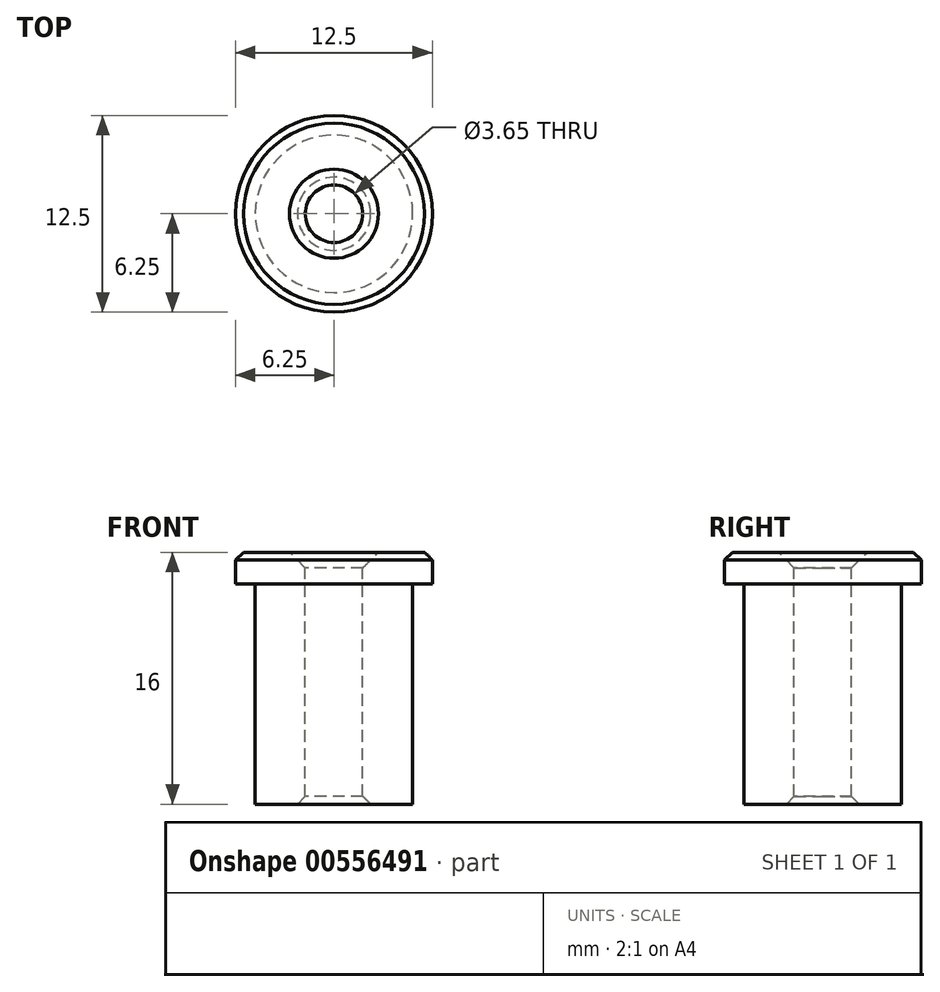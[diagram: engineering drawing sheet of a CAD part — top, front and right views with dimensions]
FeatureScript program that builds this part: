
annotation { "Feature Type Name" : "Feature", "Feature Type Description" : "" }
export const myFeature = defineFeature(function(context is Context, id is Id, definition is map)
    precondition{}
    {
        {
            var Q0;
            Q0=qCreatedBy(makeId("Top.planeOp"),FACE);
            var sketch = newSketch(context, id + "F0", { "sketchPlane" : qUnion([Q0])});
            skCircle(sketch, "E0", {"center": v(0, 0) * mm, "radius": 6.25 * mm});
            skCircle(sketch, "E1", {"center": v(0, 0) * mm, "radius": 1.82 * mm});
            skSolve(sketch);
        }
        {
            var Q0;
            Q0 = qSketchRegion(id + "F0", true);
            extrude(context, id + "F1", {"entities" : qUnion([Q0]), "oppositeDirection" : true, "depth" : 16 * mm, "offsetDistance" : 25 * mm});
        }
        {
            var Q0;
            Q0=makeQuery(id+"F1.opExtrude","CAP_EDGE",EDGE,{"disambiguationData":[OSD([sQuery(id+"F0.wireOp",EDGE,"E1")])],"isStart":true});
            chamfer(context, id + "F2", {"entities" : qUnion([Q0]), "width" : 1 * mm, "tangentPropagation" : true});
        }
        {
            var Q0;
            Q0=makeQuery(id+"F1.opExtrude","CAP_FACE",FACE,{"disambiguationData":[OSD([sQuery(id+"F0.wireOp",EDGE,"E0"),sQuery(id+"F0.wireOp",EDGE,"E1")])],"isStart":false});
            var sketch = newSketch(context, id + "F3", { "sketchPlane" : qUnion([Q0])});
            skCircle(sketch, "E2", {"center": v(0, 0) * mm, "radius": 5 * mm});
            skSolve(sketch);
        }
        {
            var Q0;
            Q0=makeQuery(id+"F3.imprint","IMPRINT",FACE,{"disambiguationData":[TD([[makeQuery(id+"F3.imprint","IMPRINT",EDGE,{"derivedFrom":sQuery(id+"F3.wireOp",EDGE,"E2")}),-1.0]])]});
            extrude(context, id + "F4", {"entities" : qUnion([Q0]), "operationType" : NewBodyOperationType.REMOVE, "oppositeDirection" : true, "depth" : 14 * mm, "offsetDistance" : 25 * mm});
        }
        {
            var Q0;
            Q0=makeQuery(id+"F4.boolean.opBoolean","COPY",EDGE,{"derivedFrom":makeQuery(id+"F4.opExtrude","CAP_EDGE",EDGE,{"disambiguationData":[OSD([sQuery(id+"F3.wireOp",EDGE,"E2")])],"isStart":true})});
            var Q1;
            Q1=makeQuery(id+"F1.opExtrude","CAP_EDGE",EDGE,{"disambiguationData":[OSD([sQuery(id+"F0.wireOp",EDGE,"E1")])],"isStart":false});
            var Q2;
            Q2=makeQuery(id+"F1.opExtrude","CAP_EDGE",EDGE,{"disambiguationData":[OSD([sQuery(id+"F0.wireOp",EDGE,"E0")])],"isStart":true});
            chamfer(context, id + "F5", {"entities" : qUnion([Q0, Q1, Q2]), "width" : 0.5 * mm, "tangentPropagation" : true});
        }
    });
